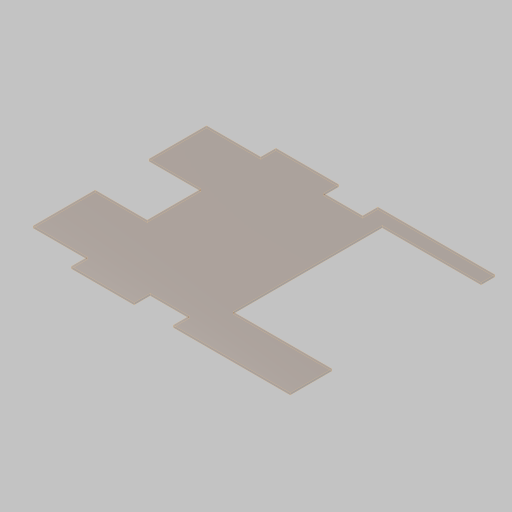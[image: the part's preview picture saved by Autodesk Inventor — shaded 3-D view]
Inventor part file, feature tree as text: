
AUTODESK INVENTOR PART (.ipt)
format: ipt  version: 2023.5 (Build 275446000, 446)  size: 264,704 bytes
history: native  units: in
note: dims shown in document units (in); Inventor stores cm internally (conversion verified against a paired STEP export)
features: sketch x5, other x3, projected_geometry x3, sheet_metal_op x1, extrude x1
ambient origin geometry x8: Origin, YZ Plane, XZ Plane, XY Plane, X Axis, Y Axis, Z Axis, Center Point
bodies: Solid1 (feature_tree)
feature tree (13):
  sheet_metal_op  "Face1"
  sketch  "Sketch3"  dims[d2=0.12in]
  extrude  "Extrusion1"  Depth=28.0in
  sketch  "Sketch1"  dims[d0=18.5in d1=28.0in]
  other  "Plate1"
  sketch  "Sketch4"  dims[d3=8.25in]
  projected_geometry  "Projected Loop1"
  sketch  "Sketch5"  dims[d4=10.0in]
  sketch  "Sketch6"  dims[d5=45.0deg d6=2.4in d9=2.75in d10=0.12in d11=0.0in d12=45.0deg d13=8.25in d14=9.0in d15=2.75in d16=2.4in d17=6.75in d18=4.5in d19=0.25in d21=4.0in d22=1.0in d23=0.1in d26=5.7in d31=0.5in d32=4.5in d33=6.75in d34=0.25in d35=4.0in d36=1.0in d37=0.1in d38=3.0in d39=1.4in d40=1.7in d41=0.1in d42=1.0in d43=0.75in d44=1.0in d45=0.75in d46=0.75in d47=1.0in d48=0.75in d49=1.0in d50=0.12in d51=0.0in d52=1.75in d53=1.0in d54=3.5in d55=1.75in d56=1.0in d57=3.5in d58=1.0in d59=0.125in d60=3.125in d61=2.25in d62=11.0in d63=1.0in d64=0.0in]
  other  "Cut1"
  other  "Cut2"
  projected_geometry  "Project Cut Edges1"
  projected_geometry  "Project Cut Edges2"
